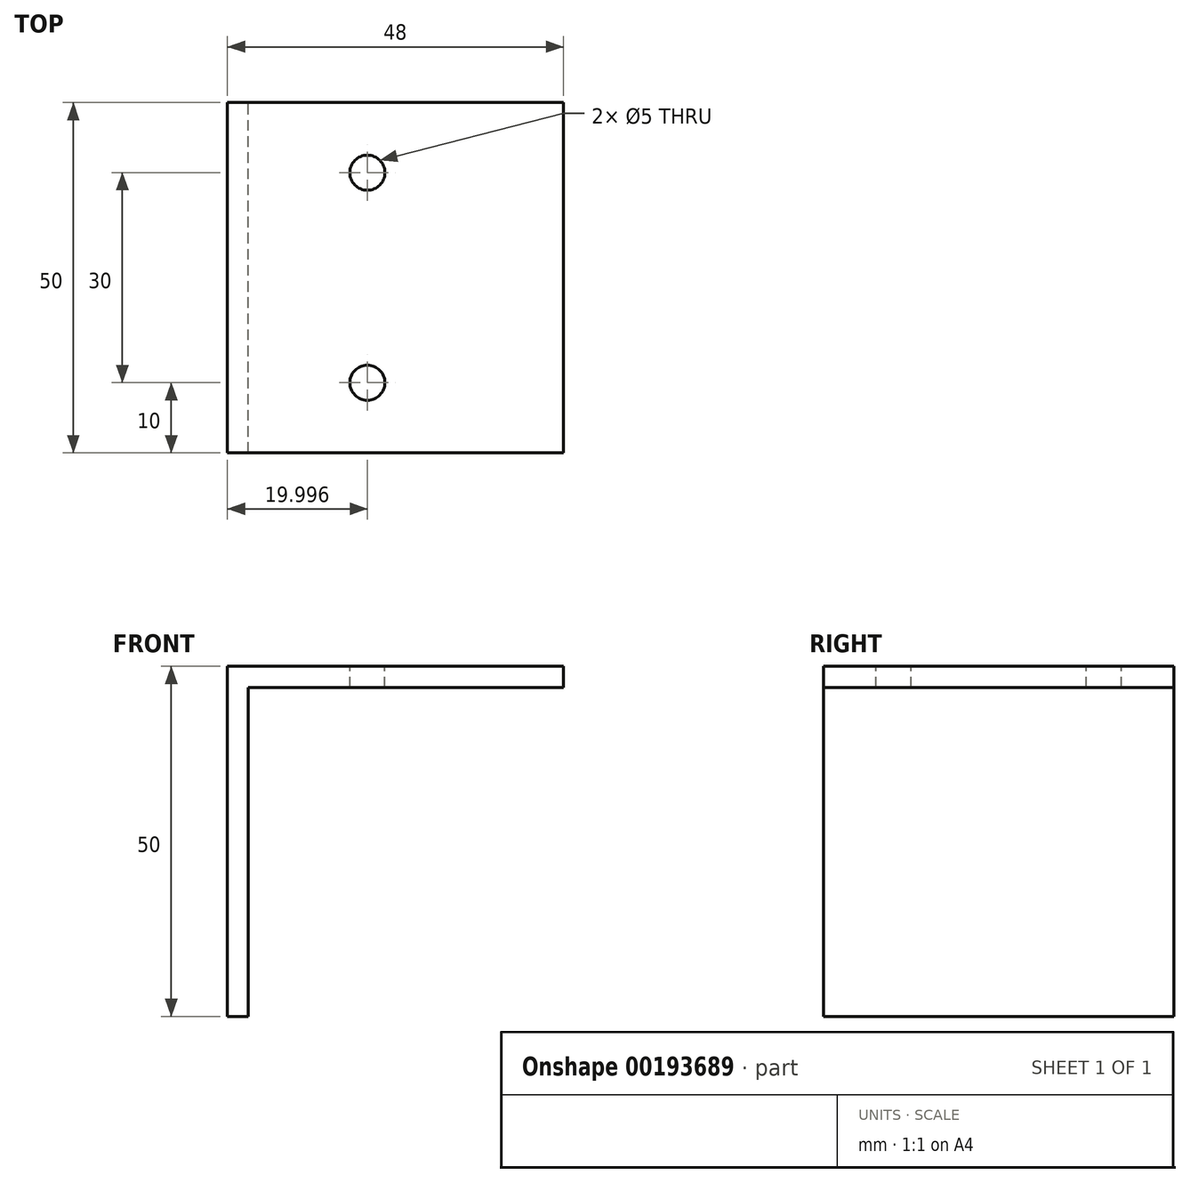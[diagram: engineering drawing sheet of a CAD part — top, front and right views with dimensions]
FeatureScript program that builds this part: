
annotation { "Feature Type Name" : "Feature", "Feature Type Description" : "" }
export const myFeature = defineFeature(function(context is Context, id is Id, definition is map)
    precondition{}
    {
        {
            var Q0;
            Q0=qCreatedBy(makeId("Front.planeOp"),FACE);
            var sketch = newSketch(context, id + "F0", { "sketchPlane" : qUnion([Q0])});
            skLineSegment(sketch, "E0", {"start": v(-38.32, 24.79) * mm, "end": v(-38.32, -25.21) * mm});
            skLineSegment(sketch, "E1", {"start": v(-38.32, -25.21) * mm, "end": v(-35.32, -25.21) * mm});
            skLineSegment(sketch, "E2", {"start": v(-35.32, -25.21) * mm, "end": v(-35.32, 21.79) * mm});
            skLineSegment(sketch, "E3", {"start": v(-35.32, 21.79) * mm, "end": v(9.68, 21.79) * mm});
            skLineSegment(sketch, "E4", {"start": v(9.68, 21.79) * mm, "end": v(9.68, 24.79) * mm});
            skLineSegment(sketch, "E5", {"start": v(9.68, 24.79) * mm, "end": v(-38.32, 24.79) * mm});
            skSolve(sketch);
        }
        {
            var Q0;
            Q0=makeQuery(id+"F0.imprint","IMPRINT",FACE,{"disambiguationData":[TD([[makeQuery(id+"F0.imprint","IMPRINT",EDGE,{"derivedFrom":sQuery(id+"F0.wireOp",EDGE,"E0")}),1.0]])]});
            extrude(context, id + "F1", {"entities" : qUnion([Q0]), "depth" : 50 * mm});
        }
        {
            var Q0;
            Q0=makeQuery(id+"F1.opExtrude","SWEPT_FACE",FACE,{"disambiguationData":[OSD([sQuery(id+"F0.wireOp",EDGE,"E5")])]});
            var sketch = newSketch(context, id + "F2", { "sketchPlane" : qUnion([Q0])});
            skCircle(sketch, "E6", {"center": v(-18.32, -40) * mm, "radius": 2.5 * mm});
            skCircle(sketch, "E7", {"center": v(-18.32, -10) * mm, "radius": 2.5 * mm});
            skSolve(sketch);
        }
        {
            var Q0;
            Q0=makeQuery(id+"F2.imprint","IMPRINT",FACE,{"disambiguationData":[TD([[makeQuery(id+"F2.imprint","IMPRINT",EDGE,{"derivedFrom":sQuery(id+"F2.wireOp",EDGE,"E6")}),-1.0]])]});
            var sketch = newSketch(context, id + "F3", { "sketchPlane" : qUnion([Q0])});
            skSolve(sketch);
        }
        {
            var Q0;
            Q0 = qSketchRegion(id + "F3", true);
            var Q1;
            Q1=makeQuery(id+"F2.imprint","IMPRINT",FACE,{"disambiguationData":[TD([[makeQuery(id+"F2.imprint","IMPRINT",EDGE,{"derivedFrom":sQuery(id+"F2.wireOp",EDGE,"E6")}),1.0]])]});
            var Q2;
            Q2=makeQuery(id+"F2.imprint","IMPRINT",FACE,{"disambiguationData":[TD([[makeQuery(id+"F2.imprint","IMPRINT",EDGE,{"derivedFrom":sQuery(id+"F2.wireOp",EDGE,"E7")}),1.0]])]});
            extrude(context, id + "F4", {"entities" : qUnion([Q0, Q1, Q2]), "operationType" : NewBodyOperationType.REMOVE, "oppositeDirection" : true, "depth" : 50 * mm});
        }
    });
